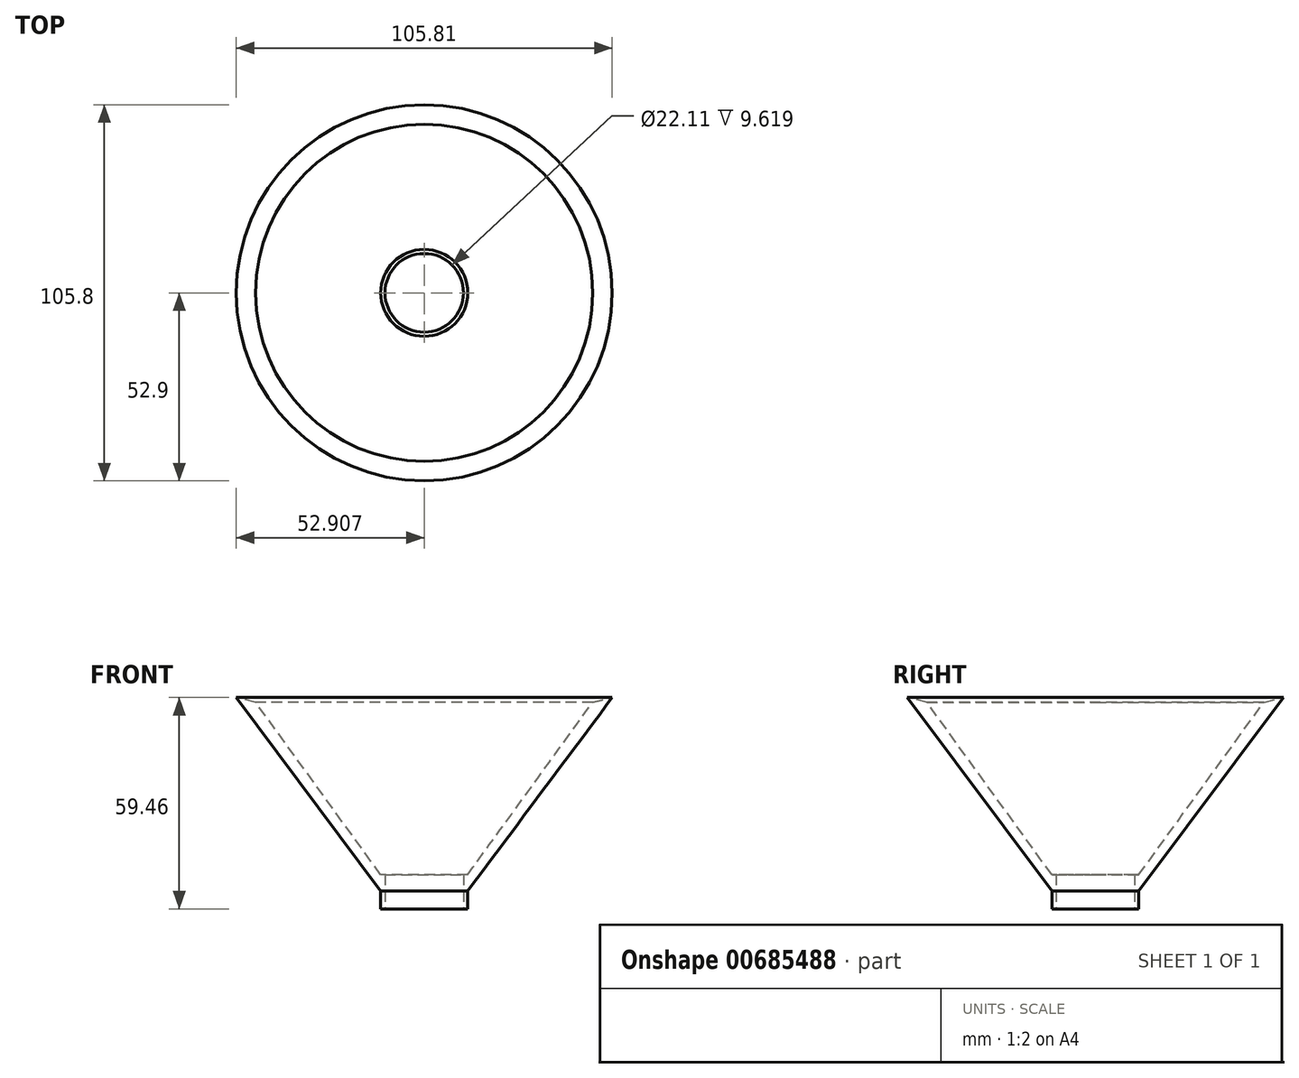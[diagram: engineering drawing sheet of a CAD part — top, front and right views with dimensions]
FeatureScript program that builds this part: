
annotation { "Feature Type Name" : "Feature", "Feature Type Description" : "" }
export const myFeature = defineFeature(function(context is Context, id is Id, definition is map)
    precondition{}
    {
        {
            var Q0;
            Q0=qCreatedBy(makeId("Front.planeOp"),FACE);
            var sketch = newSketch(context, id + "F0", { "sketchPlane" : qUnion([Q0])});
            skLineSegment(sketch, "E0", {"start": v(8.63, 37.7) * mm, "end": v(-26.56, -10.82) * mm});
            skLineSegment(sketch, "E1", {"start": v(-26.56, -10.82) * mm, "end": v(-38.8, -10.82) * mm});
            skLineSegment(sketch, "E2", {"start": v(-38.8, -10.82) * mm, "end": v(-38.8, -20.44) * mm});
            skLineSegment(sketch, "E3", {"start": v(-38.8, -20.44) * mm, "end": v(-26.56, -20.44) * mm});
            skLineSegment(sketch, "E4", {"start": v(-26.56, -20.44) * mm, "end": v(-26.56, -15.41) * mm});
            skLineSegment(sketch, "E5", {"start": v(-26.56, -15.41) * mm, "end": v(14.1, 39.02) * mm});
            skLineSegment(sketch, "E6", {"start": v(14.1, 39.02) * mm, "end": v(8.63, 37.7) * mm});
            skSolve(sketch);
        }
        {
            var Q0;
            Q0 = qSketchRegion(id + "F0", true);
            var Q1;
            Q1=sQuery(id+"F0.wireOp",EDGE,"E2");
            revolve(context, id + "F1", {"surfaceOperationType" : NewSurfaceOperationType.NEW, "entities" : qUnion([Q0]), "axis" : qUnion([Q1]), "revolveType" : RevolveType.FULL});
        }
        {
            var Q0;
            Q0=makeQuery(id+"F1.opRevolve","SWEPT_FACE",FACE,{"disambiguationData":[OSD([sQuery(id+"F0.wireOp",EDGE,"E3")])]});
            var sketch = newSketch(context, id + "F2", { "sketchPlane" : qUnion([Q0])});
            skCircle(sketch, "E7", {"center": v(-38.8, 0) * mm, "radius": 11.05 * mm});
            skSolve(sketch);
        }
        {
            var Q0;
            Q0=makeQuery(id+"F2.imprint","IMPRINT",FACE,{"disambiguationData":[TD([[makeQuery(id+"F2.imprint","IMPRINT",EDGE,{"derivedFrom":sQuery(id+"F2.wireOp",EDGE,"E7")}),1.0]])]});
            extrude(context, id + "F3", {"entities" : qUnion([Q0]), "operationType" : NewBodyOperationType.REMOVE, "oppositeDirection" : true, "depth" : 25.4 * mm, "offsetDistance" : 25.4 * mm});
        }
    });
